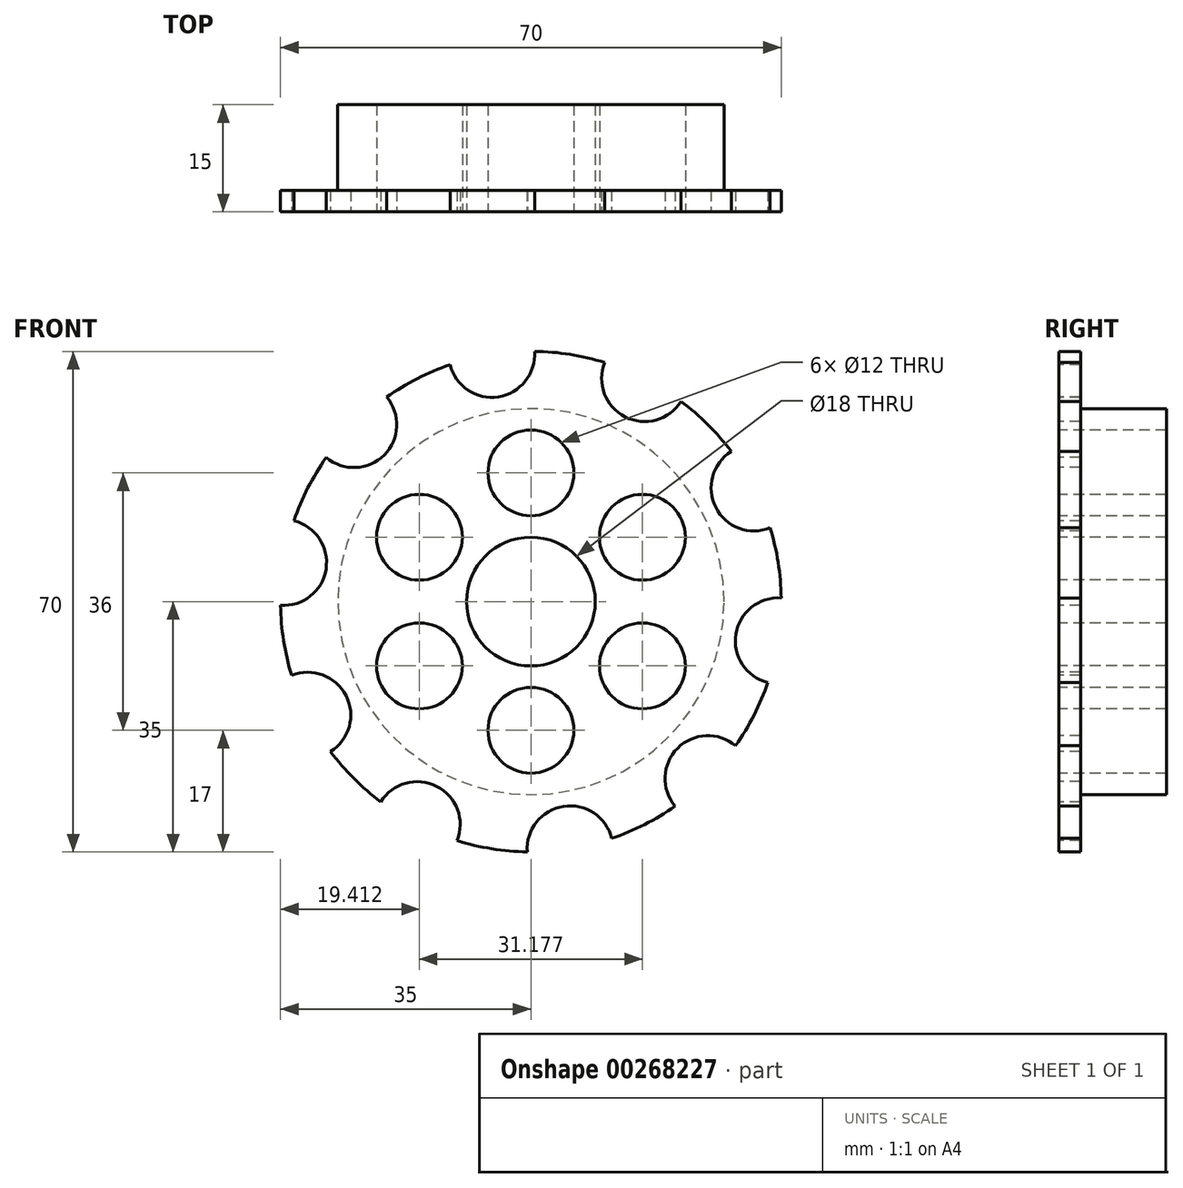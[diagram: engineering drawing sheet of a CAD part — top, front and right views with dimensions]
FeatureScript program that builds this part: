
annotation { "Feature Type Name" : "Feature", "Feature Type Description" : "" }
export const myFeature = defineFeature(function(context is Context, id is Id, definition is map)
    precondition{}
    {
        {
            var Q0;
            Q0=qCreatedBy(makeId("Front.planeOp"),FACE);
            var sketch = newSketch(context, id + "F0", { "sketchPlane" : qUnion([Q0])});
            skCircle(sketch, "E0", {"center": v(0, 0) * mm, "radius": 27 * mm});
            skSolve(sketch);
        }
        {
            var Q0;
            Q0=makeQuery(id+"F0.imprint","IMPRINT",FACE,{"disambiguationData":[TD([[makeQuery(id+"F0.imprint","IMPRINT",EDGE,{"derivedFrom":sQuery(id+"F0.wireOp",EDGE,"E0")}),1.0]])]});
            extrude(context, id + "F1", {"entities" : qUnion([Q0]), "oppositeDirection" : true, "depth" : 15 * mm});
        }
        {
            var Q0;
            Q0=makeQuery(id+"F1.opExtrude","CAP_FACE",FACE,{"disambiguationData":[OSD([sQuery(id+"F0.wireOp",EDGE,"E0")])],"isStart":true});
            var sketch = newSketch(context, id + "F2", { "sketchPlane" : qUnion([Q0])});
            skCircle(sketch, "E1", {"center": v(0, 0) * mm, "radius": 27 * mm});
            skCircle(sketch, "E2", {"center": v(0, 0) * mm, "radius": 35 * mm});
            skSolve(sketch);
        }
        {
            var Q0;
            Q0=makeQuery(id+"F2.imprint","IMPRINT",FACE,{"disambiguationData":[TD([[makeQuery(id+"F2.imprint","IMPRINT",EDGE,{"derivedFrom":sQuery(id+"F2.wireOp",EDGE,"E1")}),-1.0]])]});
            extrude(context, id + "F3", {"entities" : qUnion([Q0]), "operationType" : NewBodyOperationType.ADD, "oppositeDirection" : true, "depth" : 3 * mm});
        }
        {
            var Q0;
            Q0=makeQuery(id+"F3.boolean.opBoolean","MERGE",FACE,{"derivedFrom":[makeQuery(id+"F1.opExtrude","CAP_FACE",FACE,{"disambiguationData":[OSD([sQuery(id+"F0.wireOp",EDGE,"E0")])],"isStart":true}),makeQuery(id+"F3.opExtrude","CAP_FACE",FACE,{"disambiguationData":[OSD([sQuery(id+"F2.wireOp",EDGE,"E1"),sQuery(id+"F2.wireOp",EDGE,"E2")])],"isStart":true})]});
            var sketch = newSketch(context, id + "F4", { "sketchPlane" : qUnion([Q0])});
            skCircle(sketch, "E3", {"center": v(0, 0) * mm, "radius": 9 * mm});
            skSolve(sketch);
        }
        {
            var Q0;
            Q0=makeQuery(id+"F4.imprint","IMPRINT",FACE,{"disambiguationData":[TD([[makeQuery(id+"F4.imprint","IMPRINT",EDGE,{"derivedFrom":sQuery(id+"F4.wireOp",EDGE,"E3")}),1.0]])]});
            extrude(context, id + "F5", {"entities" : qUnion([Q0]), "operationType" : NewBodyOperationType.REMOVE, "endBound" : BoundingType.THROUGH_ALL, "oppositeDirection" : true, "depth" : 25 * mm});
        }
        {
            var Q0;
            Q0=makeQuery(id+"F3.boolean.opBoolean","MERGE",FACE,{"derivedFrom":[makeQuery(id+"F1.opExtrude","CAP_FACE",FACE,{"disambiguationData":[OSD([sQuery(id+"F0.wireOp",EDGE,"E0")])],"isStart":true}),makeQuery(id+"F3.opExtrude","CAP_FACE",FACE,{"disambiguationData":[OSD([sQuery(id+"F2.wireOp",EDGE,"E1"),sQuery(id+"F2.wireOp",EDGE,"E2")])],"isStart":true})]});
            var sketch = newSketch(context, id + "F6", { "sketchPlane" : qUnion([Q0])});
            skCircle(sketch, "E4", {"center": v(0, 18) * mm, "radius": 6 * mm});
            skCircle(sketch, "E5.1.0", {"center": v(-15.59, 9) * mm, "radius": 6 * mm});
            skCircle(sketch, "E5.2.0", {"center": v(-15.59, -9) * mm, "radius": 6 * mm});
            skCircle(sketch, "E5.3.0", {"center": v(0, -18) * mm, "radius": 6 * mm});
            skPoint(sketch, "E5.center", {"position": v(0, 0) * mm});
            skCircle(sketch, "E6", {"center": v(-24.75, 24.75) * mm, "radius": 6 * mm});
            skLineSegment(sketch, "E7", {"start": v(-24.75, 24.75) * mm, "end": v(0, 0) * mm, "construction": true});
            skCircle(sketch, "E8.1.0", {"center": v(-34.57, 5.48) * mm, "radius": 6 * mm});
            skCircle(sketch, "E8.2.0", {"center": v(-31.19, -15.89) * mm, "radius": 6 * mm});
            skCircle(sketch, "E8.3.0", {"center": v(-15.89, -31.19) * mm, "radius": 6 * mm});
            skCircle(sketch, "E8.4.0", {"center": v(5.48, -34.57) * mm, "radius": 6 * mm});
            skCircle(sketch, "E8.5.0", {"center": v(24.75, -24.75) * mm, "radius": 6 * mm});
            skCircle(sketch, "E8.6.0", {"center": v(34.57, -5.48) * mm, "radius": 6 * mm});
            skCircle(sketch, "E8.7.0", {"center": v(31.19, 15.89) * mm, "radius": 6 * mm});
            skCircle(sketch, "E8.8.0", {"center": v(15.89, 31.19) * mm, "radius": 6 * mm});
            skCircle(sketch, "E8.9.0", {"center": v(-5.48, 34.57) * mm, "radius": 6 * mm});
            skCircle(sketch, "E9.1.4.0", {"center": v(15.59, -9) * mm, "radius": 6 * mm});
            skCircle(sketch, "E10.1.5.0", {"center": v(15.59, 9) * mm, "radius": 6 * mm});
            skSolve(sketch);
        }
        {
            var Q0;
            Q0=makeQuery(id+"F6.imprint","IMPRINT",FACE,{"disambiguationData":[TD([[makeQuery(id+"F6.imprint","IMPRINT",EDGE,{"derivedFrom":sQuery(id+"F6.wireOp",EDGE,"E4")}),1.0]])]});
            var Q1;
            Q1=makeQuery(id+"F6.imprint","IMPRINT",FACE,{"disambiguationData":[TD([[makeQuery(id+"F6.imprint","IMPRINT",EDGE,{"derivedFrom":sQuery(id+"F6.wireOp",EDGE,"E5.3.0")}),1.0]])]});
            var Q2;
            Q2=makeQuery(id+"F6.imprint","IMPRINT",FACE,{"disambiguationData":[TD([[makeQuery(id+"F6.imprint","IMPRINT",EDGE,{"derivedFrom":sQuery(id+"F6.wireOp",EDGE,"E5.2.0")}),1.0]])]});
            var Q3;
            Q3=makeQuery(id+"F6.imprint","IMPRINT",FACE,{"disambiguationData":[TD([[makeQuery(id+"F6.imprint","IMPRINT",EDGE,{"derivedFrom":sQuery(id+"F6.wireOp",EDGE,"E5.1.0")}),1.0]])]});
            var Q4;
            {var subQ0=sQuery(id+"F6.wireOp",EDGE,"E6");var subQ1=makeQuery(id+"F3.opExtrude","CAP_EDGE",EDGE,{"disambiguationData":[OSD([sQuery(id+"F2.wireOp",EDGE,"E2")])],"isStart":true});var subQ2=makeQuery(id+"F6.imprint","INTERSECT",VERTEX,{"disambiguationData":[OD(0.0)],"derivedFrom":[subQ1,subQ0]});Q4=makeQuery(id+"F6.imprint","IMPRINT",FACE,{"disambiguationData":[TD([[makeQuery(id+"F6.imprint","IMPRINT",EDGE,{"disambiguationData":[TD([[subQ2,-1.0]])],"derivedFrom":subQ0}),1.0]])]});}
            var Q5;
            {var subQ0=sQuery(id+"F6.wireOp",EDGE,"E8.9.0");var subQ1=makeQuery(id+"F3.opExtrude","CAP_EDGE",EDGE,{"disambiguationData":[OSD([sQuery(id+"F2.wireOp",EDGE,"E2")])],"isStart":true});var subQ2=makeQuery(id+"F6.imprint","INTERSECT",VERTEX,{"disambiguationData":[OD(0.0)],"derivedFrom":[subQ1,subQ0]});Q5=makeQuery(id+"F6.imprint","IMPRINT",FACE,{"disambiguationData":[TD([[makeQuery(id+"F6.imprint","IMPRINT",EDGE,{"disambiguationData":[TD([[subQ2,-1.0]])],"derivedFrom":subQ0}),1.0]])]});}
            var Q6;
            {var subQ0=sQuery(id+"F6.wireOp",EDGE,"E8.8.0");var subQ1=makeQuery(id+"F3.opExtrude","CAP_EDGE",EDGE,{"disambiguationData":[OSD([sQuery(id+"F2.wireOp",EDGE,"E2")])],"isStart":true});var subQ2=makeQuery(id+"F6.imprint","INTERSECT",VERTEX,{"disambiguationData":[OD(0.0)],"derivedFrom":[subQ1,subQ0]});Q6=makeQuery(id+"F6.imprint","IMPRINT",FACE,{"disambiguationData":[TD([[makeQuery(id+"F6.imprint","IMPRINT",EDGE,{"disambiguationData":[TD([[subQ2,-1.0]])],"derivedFrom":subQ0}),1.0]])]});}
            var Q7;
            {var subQ0=sQuery(id+"F6.wireOp",EDGE,"E8.7.0");var subQ1=makeQuery(id+"F3.opExtrude","CAP_EDGE",EDGE,{"disambiguationData":[OSD([sQuery(id+"F2.wireOp",EDGE,"E2")])],"isStart":true});var subQ2=makeQuery(id+"F6.imprint","INTERSECT",VERTEX,{"disambiguationData":[OD(0.0)],"derivedFrom":[subQ1,subQ0]});Q7=makeQuery(id+"F6.imprint","IMPRINT",FACE,{"disambiguationData":[TD([[makeQuery(id+"F6.imprint","IMPRINT",EDGE,{"disambiguationData":[TD([[subQ2,-1.0]])],"derivedFrom":subQ0}),1.0]])]});}
            var Q8;
            {var subQ0=sQuery(id+"F6.wireOp",EDGE,"E8.6.0");var subQ1=makeQuery(id+"F3.opExtrude","CAP_EDGE",EDGE,{"disambiguationData":[OSD([sQuery(id+"F2.wireOp",EDGE,"E2")])],"isStart":true});var subQ2=makeQuery(id+"F6.imprint","INTERSECT",VERTEX,{"disambiguationData":[OD(0.0)],"derivedFrom":[subQ1,subQ0]});Q8=makeQuery(id+"F6.imprint","IMPRINT",FACE,{"disambiguationData":[TD([[makeQuery(id+"F6.imprint","IMPRINT",EDGE,{"disambiguationData":[TD([[subQ2,1.0]])],"derivedFrom":subQ0}),1.0]])]});}
            var Q9;
            {var subQ0=sQuery(id+"F6.wireOp",EDGE,"E8.5.0");var subQ1=makeQuery(id+"F3.opExtrude","CAP_EDGE",EDGE,{"disambiguationData":[OSD([sQuery(id+"F2.wireOp",EDGE,"E2")])],"isStart":true});var subQ2=makeQuery(id+"F6.imprint","INTERSECT",VERTEX,{"disambiguationData":[OD(0.0)],"derivedFrom":[subQ1,subQ0]});Q9=makeQuery(id+"F6.imprint","IMPRINT",FACE,{"disambiguationData":[TD([[makeQuery(id+"F6.imprint","IMPRINT",EDGE,{"disambiguationData":[TD([[subQ2,1.0]])],"derivedFrom":subQ0}),1.0]])]});}
            var Q10;
            {var subQ0=sQuery(id+"F6.wireOp",EDGE,"E8.4.0");var subQ1=makeQuery(id+"F3.opExtrude","CAP_EDGE",EDGE,{"disambiguationData":[OSD([sQuery(id+"F2.wireOp",EDGE,"E2")])],"isStart":true});var subQ2=makeQuery(id+"F6.imprint","INTERSECT",VERTEX,{"disambiguationData":[OD(0.0)],"derivedFrom":[subQ1,subQ0]});Q10=makeQuery(id+"F6.imprint","IMPRINT",FACE,{"disambiguationData":[TD([[makeQuery(id+"F6.imprint","IMPRINT",EDGE,{"disambiguationData":[TD([[subQ2,1.0]])],"derivedFrom":subQ0}),1.0]])]});}
            var Q11;
            {var subQ0=sQuery(id+"F6.wireOp",EDGE,"E8.3.0");var subQ1=makeQuery(id+"F3.opExtrude","CAP_EDGE",EDGE,{"disambiguationData":[OSD([sQuery(id+"F2.wireOp",EDGE,"E2")])],"isStart":true});var subQ2=makeQuery(id+"F6.imprint","INTERSECT",VERTEX,{"disambiguationData":[OD(0.0)],"derivedFrom":[subQ1,subQ0]});Q11=makeQuery(id+"F6.imprint","IMPRINT",FACE,{"disambiguationData":[TD([[makeQuery(id+"F6.imprint","IMPRINT",EDGE,{"disambiguationData":[TD([[subQ2,1.0]])],"derivedFrom":subQ0}),1.0]])]});}
            var Q12;
            {var subQ0=sQuery(id+"F6.wireOp",EDGE,"E8.2.0");var subQ1=makeQuery(id+"F3.opExtrude","CAP_EDGE",EDGE,{"disambiguationData":[OSD([sQuery(id+"F2.wireOp",EDGE,"E2")])],"isStart":true});var subQ2=makeQuery(id+"F6.imprint","INTERSECT",VERTEX,{"disambiguationData":[OD(0.0)],"derivedFrom":[subQ1,subQ0]});Q12=makeQuery(id+"F6.imprint","IMPRINT",FACE,{"disambiguationData":[TD([[makeQuery(id+"F6.imprint","IMPRINT",EDGE,{"disambiguationData":[TD([[subQ2,1.0]])],"derivedFrom":subQ0}),1.0]])]});}
            var Q13;
            {var subQ0=sQuery(id+"F6.wireOp",EDGE,"E8.1.0");var subQ1=makeQuery(id+"F3.opExtrude","CAP_EDGE",EDGE,{"disambiguationData":[OSD([sQuery(id+"F2.wireOp",EDGE,"E2")])],"isStart":true});var subQ2=makeQuery(id+"F6.imprint","INTERSECT",VERTEX,{"disambiguationData":[OD(0.0)],"derivedFrom":[subQ1,subQ0]});Q13=makeQuery(id+"F6.imprint","IMPRINT",FACE,{"disambiguationData":[TD([[makeQuery(id+"F6.imprint","IMPRINT",EDGE,{"disambiguationData":[TD([[subQ2,-1.0]])],"derivedFrom":subQ0}),1.0]])]});}
            var Q14;
            Q14=makeQuery(id+"F6.imprint","IMPRINT",FACE,{"disambiguationData":[TD([[makeQuery(id+"F6.imprint","IMPRINT",EDGE,{"derivedFrom":sQuery(id+"F6.wireOp",EDGE,"E10.1.5.0")}),1.0]])]});
            var Q15;
            Q15=makeQuery(id+"F6.imprint","IMPRINT",FACE,{"disambiguationData":[TD([[makeQuery(id+"F6.imprint","IMPRINT",EDGE,{"derivedFrom":sQuery(id+"F6.wireOp",EDGE,"E9.1.4.0")}),1.0]])]});
            extrude(context, id + "F7", {"entities" : qUnion([Q0, Q1, Q2, Q3, Q4, Q5, Q6, Q7, Q8, Q9, Q10, Q11, Q12, Q13, Q14, Q15]), "operationType" : NewBodyOperationType.REMOVE, "endBound" : BoundingType.THROUGH_ALL, "oppositeDirection" : true, "depth" : 25 * mm});
        }
    });
